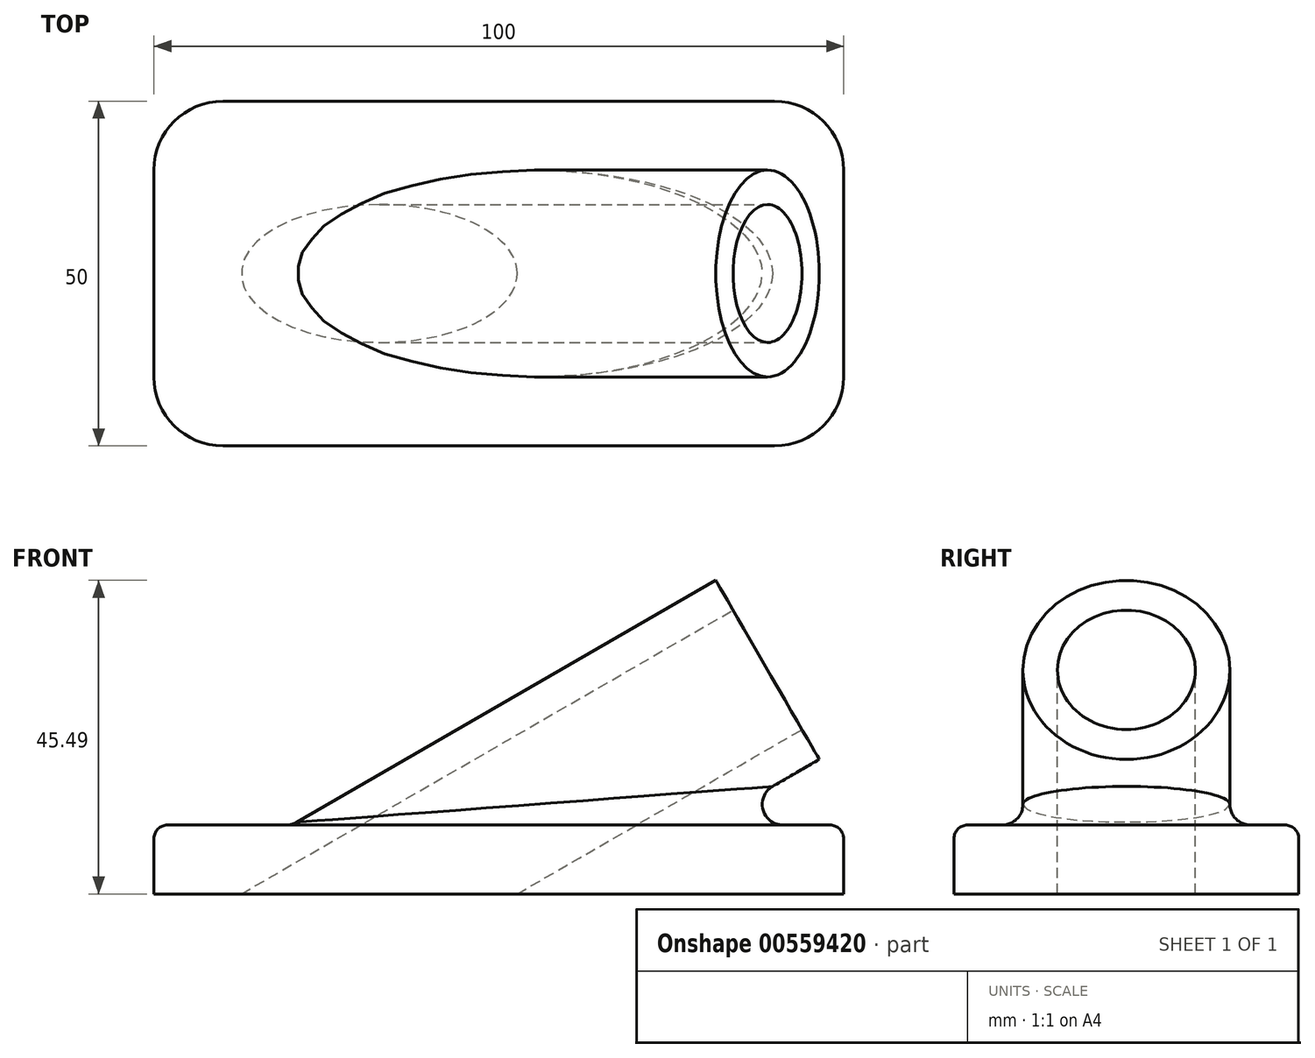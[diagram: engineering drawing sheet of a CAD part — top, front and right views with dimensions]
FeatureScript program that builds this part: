
annotation { "Feature Type Name" : "Feature", "Feature Type Description" : "" }
export const myFeature = defineFeature(function(context is Context, id is Id, definition is map)
    precondition{}
    {
        {
            var Q0;
            Q0=qCreatedBy(makeId("Top.planeOp"),FACE);
            var sketch = newSketch(context, id + "F0", { "sketchPlane" : qUnion([Q0])});
            skLineSegment(sketch, "E0.bottom", {"start": v(50, 25) * mm, "end": v(-50, 25) * mm});
            skLineSegment(sketch, "E0.top", {"start": v(50, -25) * mm, "end": v(-50, -25) * mm});
            skLineSegment(sketch, "E0.left", {"start": v(50, 25) * mm, "end": v(50, -25) * mm});
            skLineSegment(sketch, "E0.right", {"start": v(-50, 25) * mm, "end": v(-50, -25) * mm});
            skPoint(sketch, "E0.middle", {"position": v(0, 0) * mm});
            skSolve(sketch);
        }
        {
            var Q0;
            Q0 = qSketchRegion(id + "F0", true);
            extrude(context, id + "F1", {"entities" : qUnion([Q0]), "depth" : 10 * mm, "offsetDistance" : 25 * mm});
        }
        {
            var Q0;
            Q0=qCreatedBy(makeId("Front.planeOp"),FACE);
            var sketch = newSketch(context, id + "F2", { "sketchPlane" : qUnion([Q0])});
            skLineSegment(sketch, "E1", {"start": v(0, 10) * mm, "end": v(38.97, 32.5) * mm});
            skLineSegment(sketch, "E2", {"start": v(38.97, 32.5) * mm, "end": v(46.47, 19.5) * mm});
            skLineSegment(sketch, "E3", {"start": v(46.47, 19.5) * mm, "end": v(30, 10) * mm});
            skLineSegment(sketch, "E4", {"start": v(38.97, 32.5) * mm, "end": v(31.47, 45.5) * mm});
            skLineSegment(sketch, "E5", {"start": v(31.47, 45.5) * mm, "end": v(-30, 10) * mm});
            skLineSegment(sketch, "E6", {"start": v(-30, 10) * mm, "end": v(30, 10) * mm});
            skSolve(sketch);
        }
        {
            var Q0;
            Q0 = qSketchRegion(id + "F2", true);
            extrude(context, id + "F3", {"entities" : qUnion([Q0]), "operationType" : NewBodyOperationType.ADD, "endBound" : BoundingType.SYMMETRIC, "depth" : 30 * mm, "offsetDistance" : 25 * mm});
        }
        {
            var Q0;
            Q0=makeQuery(id+"F3.opExtrude","CAP_EDGE",EDGE,{"disambiguationData":[OSD([sQuery(id+"F2.wireOp",EDGE,"E5")])],"isStart":false});
            var Q1;
            Q1=makeQuery(id+"F3.opExtrude","CAP_EDGE",EDGE,{"disambiguationData":[OSD([sQuery(id+"F2.wireOp",EDGE,"E5")])],"isStart":true});
            var Q2;
            Q2=makeQuery(id+"F3.opExtrude","CAP_EDGE",EDGE,{"disambiguationData":[OSD([sQuery(id+"F2.wireOp",EDGE,"E3")])],"isStart":false});
            var Q3;
            Q3=makeQuery(id+"F3.opExtrude","CAP_EDGE",EDGE,{"disambiguationData":[OSD([sQuery(id+"F2.wireOp",EDGE,"E3")])],"isStart":true});
            fillet(context, id + "F4", {"entities" : qUnion([Q0, Q1, Q2, Q3]), "radius" : 15 * mm, "tangentPropagation" : true, "allowEdgeOverflow" : false});
        }
        {
            var Q0;
            Q0=makeQuery(id+"F4.opFillet","BLEND_EDGE",EDGE,{"blendedFrom":[makeQuery(id+"F3.opExtrude","CAP_EDGE",EDGE,{"disambiguationData":[OSD([sQuery(id+"F2.wireOp",EDGE,"E3")])],"isStart":true}),makeQuery(id+"F1.opExtrude","CAP_FACE",FACE,{"disambiguationData":[OSD([sQuery(id+"F0.wireOp",EDGE,"E0.bottom"),sQuery(id+"F0.wireOp",EDGE,"E0.top"),sQuery(id+"F0.wireOp",EDGE,"E0.left"),sQuery(id+"F0.wireOp",EDGE,"E0.right")])],"isStart":false})],"blendedInto":[makeQuery(id+"F1.opExtrude","CAP_FACE",FACE,{"disambiguationData":[OSD([sQuery(id+"F0.wireOp",EDGE,"E0.bottom"),sQuery(id+"F0.wireOp",EDGE,"E0.top"),sQuery(id+"F0.wireOp",EDGE,"E0.left"),sQuery(id+"F0.wireOp",EDGE,"E0.right")])],"isStart":false})]});
            fillet(context, id + "F5", {"entities" : qUnion([Q0]), "radius" : 3 * mm, "tangentPropagation" : true, "allowEdgeOverflow" : false});
        }
        {
            var Q0;
            Q0=makeQuery(id+"F3.opExtrude","SWEPT_FACE",FACE,{"disambiguationData":[OSD([sQuery(id+"F2.wireOp",EDGE,"E2"),sQuery(id+"F2.wireOp",EDGE,"E4")])]});
            var sketch = newSketch(context, id + "F6", { "sketchPlane" : qUnion([Q0])});
            skCircle(sketch, "E7", {"center": v(0, 8.66) * mm, "radius": 10 * mm});
            skSolve(sketch);
        }
        {
            var Q0;
            Q0 = qSketchRegion(id + "F6", true);
            extrude(context, id + "F7", {"entities" : qUnion([Q0]), "operationType" : NewBodyOperationType.REMOVE, "endBound" : BoundingType.THROUGH_ALL, "oppositeDirection" : true, "depth" : 25 * mm, "offsetDistance" : 25 * mm});
        }
        {
            var Q0;
            Q0=makeQuery(id+"F1.opExtrude","CAP_EDGE",EDGE,{"disambiguationData":[OSD([sQuery(id+"F0.wireOp",EDGE,"E0.top")])],"isStart":false});
            var Q1;
            Q1=makeQuery(id+"F1.opExtrude","CAP_EDGE",EDGE,{"disambiguationData":[OSD([sQuery(id+"F0.wireOp",EDGE,"E0.right")])],"isStart":false});
            var Q2;
            Q2=makeQuery(id+"F1.opExtrude","CAP_EDGE",EDGE,{"disambiguationData":[OSD([sQuery(id+"F0.wireOp",EDGE,"E0.left")])],"isStart":false});
            var Q3;
            Q3=makeQuery(id+"F1.opExtrude","CAP_EDGE",EDGE,{"disambiguationData":[OSD([sQuery(id+"F0.wireOp",EDGE,"E0.bottom")])],"isStart":false});
            fillet(context, id + "F8", {"entities" : qUnion([Q0, Q1, Q2, Q3]), "radius" : 2 * mm, "tangentPropagation" : true, "allowEdgeOverflow" : false});
        }
        {
            var Q0;
            Q0=makeQuery(id+"F1.opExtrude","SWEPT_EDGE",EDGE,{"disambiguationData":[OSD([sQuery(id+"F0.wireOp",EDGE,"E0.top"),sQuery(id+"F0.wireOp",EDGE,"E0.right")])]});
            var Q1;
            Q1=makeQuery(id+"F1.opExtrude","SWEPT_EDGE",EDGE,{"disambiguationData":[OSD([sQuery(id+"F0.wireOp",EDGE,"E0.top"),sQuery(id+"F0.wireOp",EDGE,"E0.left")])]});
            var Q2;
            Q2=makeQuery(id+"F1.opExtrude","SWEPT_EDGE",EDGE,{"disambiguationData":[OSD([sQuery(id+"F0.wireOp",EDGE,"E0.bottom"),sQuery(id+"F0.wireOp",EDGE,"E0.right")])]});
            var Q3;
            Q3=makeQuery(id+"F1.opExtrude","SWEPT_EDGE",EDGE,{"disambiguationData":[OSD([sQuery(id+"F0.wireOp",EDGE,"E0.bottom"),sQuery(id+"F0.wireOp",EDGE,"E0.left")])]});
            fillet(context, id + "F9", {"entities" : qUnion([Q0, Q1, Q2, Q3]), "radius" : 10 * mm, "tangentPropagation" : true, "allowEdgeOverflow" : false});
        }
    });
